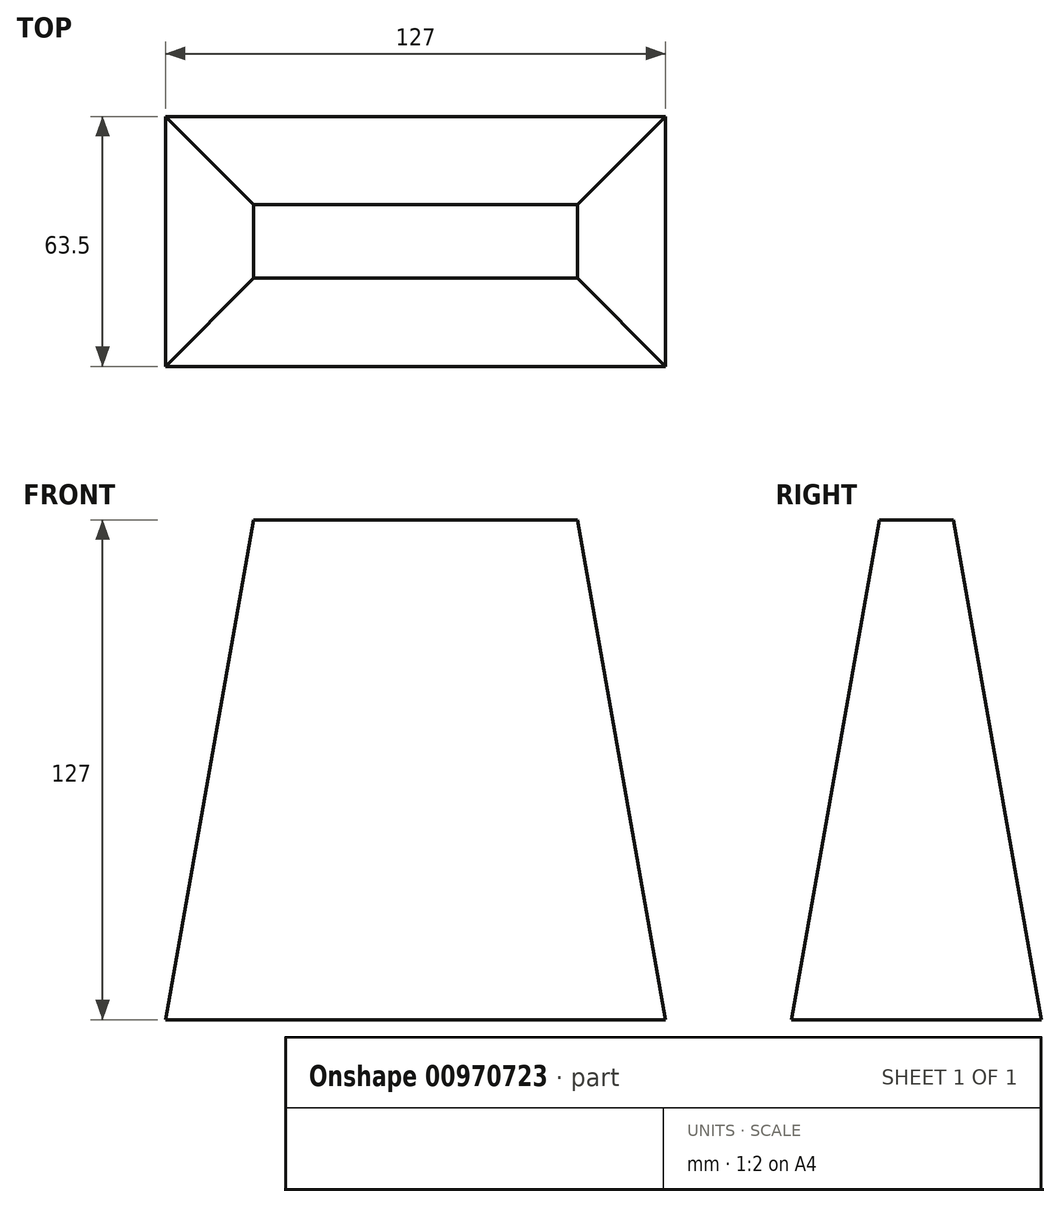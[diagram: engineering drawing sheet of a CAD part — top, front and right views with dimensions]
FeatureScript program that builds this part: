
annotation { "Feature Type Name" : "Feature", "Feature Type Description" : "" }
export const myFeature = defineFeature(function(context is Context, id is Id, definition is map)
    precondition{}
    {
        {
            var Q0;
            Q0=qCreatedBy(makeId("Top.planeOp"),FACE);
            var sketch = newSketch(context, id + "F0", { "sketchPlane" : qUnion([Q0])});
            skLineSegment(sketch, "E0.bottom", {"start": v(-3.57, 0) * mm, "end": v(123.43, 0) * mm});
            skLineSegment(sketch, "E0.top", {"start": v(-3.57, -63.5) * mm, "end": v(123.43, -63.5) * mm});
            skLineSegment(sketch, "E0.left", {"start": v(-3.57, 0) * mm, "end": v(-3.57, -63.5) * mm});
            skLineSegment(sketch, "E0.right", {"start": v(123.43, 0) * mm, "end": v(123.43, -63.5) * mm});
            skSolve(sketch);
        }
        {
            var Q0;
            Q0=makeQuery(id+"F0.imprint","IMPRINT",FACE,{"disambiguationData":[TD([[makeQuery(id+"F0.imprint","IMPRINT",EDGE,{"derivedFrom":sQuery(id+"F0.wireOp",EDGE,"E0.bottom")}),-1.0]])]});
            extrude(context, id + "F1", {"entities" : qUnion([Q0]), "depth" : 127 * mm, "offsetDistance" : 25.4 * mm, "hasDraft" : true, "draftAngle" : 10 * degree, "draftPullDirection" : true});
        }
    });
